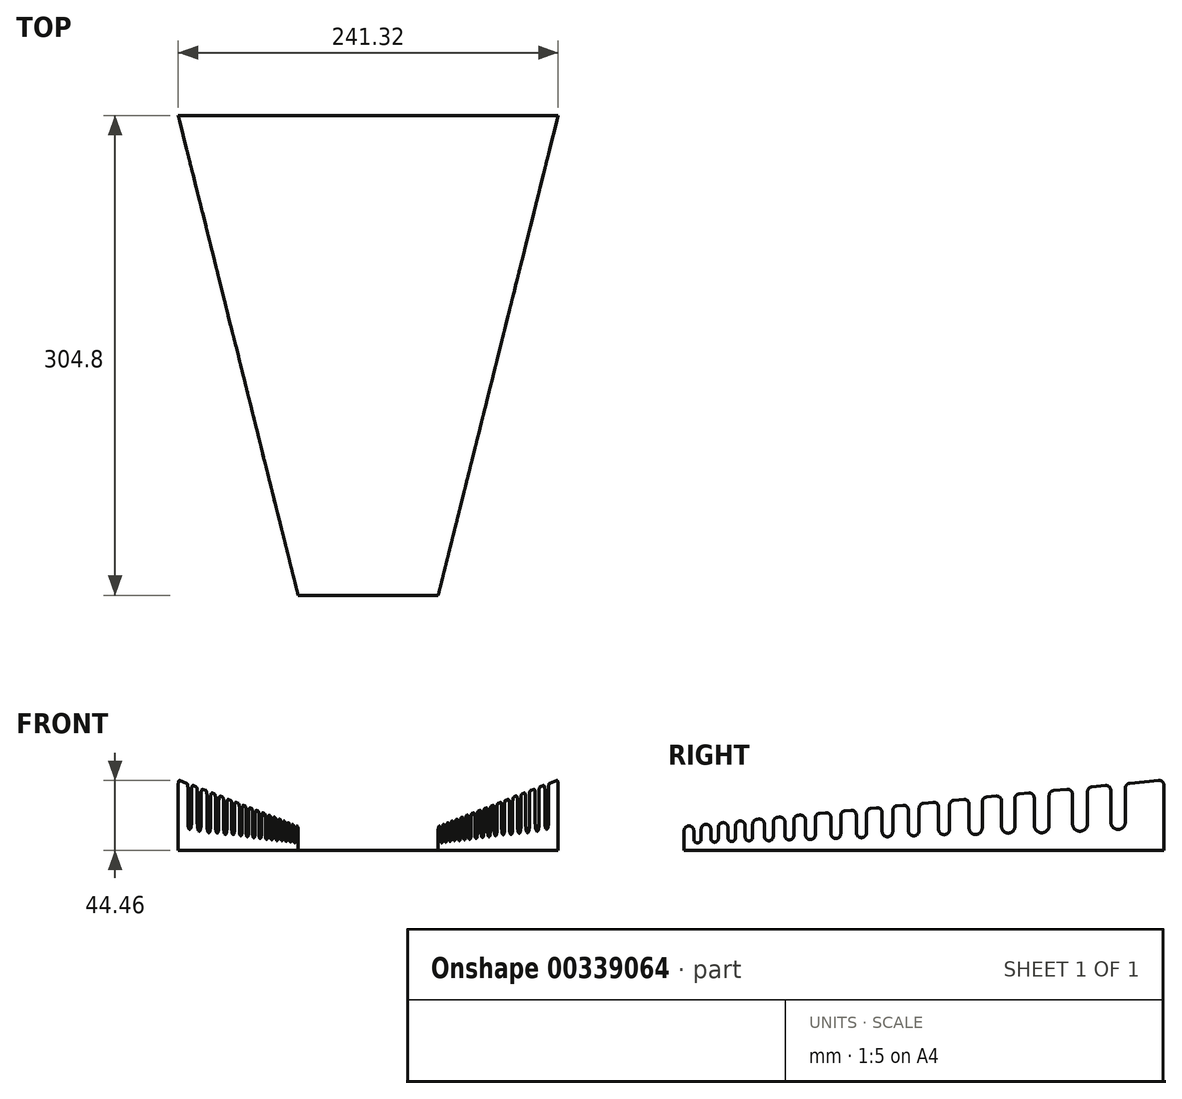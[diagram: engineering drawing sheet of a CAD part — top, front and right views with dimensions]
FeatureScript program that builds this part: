
annotation { "Feature Type Name" : "Feature", "Feature Type Description" : "" }
export const myFeature = defineFeature(function(context is Context, id is Id, definition is map)
    precondition{}
    {
        {
            var Q0;
            Q0=qCreatedBy(makeId("Top.planeOp"),FACE);
            var sketch = newSketch(context, id + "F0", { "sketchPlane" : qUnion([Q0])});
            skLineSegment(sketch, "E0", {"start": v(-44.45, 0) * mm, "end": v(44.45, 0) * mm});
            skLineSegment(sketch, "E1", {"start": v(44.45, 0) * mm, "end": v(120.65, 304.8) * mm});
            skLineSegment(sketch, "E2", {"start": v(120.65, 304.8) * mm, "end": v(-120.65, 304.8) * mm});
            skLineSegment(sketch, "E3", {"start": v(-120.65, 304.8) * mm, "end": v(-44.45, 0) * mm});
            skSolve(sketch);
        }
        {
            var Q0;
            Q0 = qSketchRegion(id + "F0", true);
            extrude(context, id + "F1", {"entities" : qUnion([Q0]), "depth" : 3 / 406.4 * mm});
        }
        {
            var Q0;
            Q0=makeQuery(id+"F1.opExtrude","SWEPT_FACE",FACE,{"disambiguationData":[OSD([sQuery(id+"F0.wireOp",EDGE,"E1")])]});
            var sketch = newSketch(context, id + "F2", { "sketchPlane" : qUnion([Q0])});
            skLineSegment(sketch, "E4", {"start": v(10.78, 0) * mm, "end": v(10.78, 12.35) * mm});
            skLineSegment(sketch, "E5", {"start": v(13.66, 15.51) * mm, "end": v(13.66, 15.51) * mm});
            skLineSegment(sketch, "E6", {"start": v(17.13, 12.35) * mm, "end": v(17.13, 7.18) * mm});
            skLineSegment(sketch, "E7", {"start": v(17.13, 7.18) * mm, "end": v(21.96, 7.37) * mm, "construction": true});
            skLineSegment(sketch, "E8", {"start": v(21.96, 7.37) * mm, "end": v(21.96, 13.4) * mm});
            skLineSegment(sketch, "E9", {"start": v(24.83, 16.56) * mm, "end": v(24.83, 16.56) * mm});
            skLineSegment(sketch, "E10", {"start": v(28.3, 13.4) * mm, "end": v(28.3, 7.62) * mm});
            skLineSegment(sketch, "E11", {"start": v(28.3, 7.62) * mm, "end": v(33.13, 7.82) * mm, "construction": true});
            skLineSegment(sketch, "E12", {"start": v(33.13, 7.82) * mm, "end": v(33.13, 14.45) * mm});
            skLineSegment(sketch, "E13", {"start": v(36.01, 17.61) * mm, "end": v(36.01, 17.61) * mm});
            skLineSegment(sketch, "E14", {"start": v(39.48, 14.45) * mm, "end": v(39.48, 8.07) * mm});
            skLineSegment(sketch, "E15", {"start": v(39.48, 8.07) * mm, "end": v(44.38, 8.27) * mm, "construction": true});
            skLineSegment(sketch, "E16", {"start": v(44.38, 8.27) * mm, "end": v(44.38, 15.5) * mm});
            skLineSegment(sketch, "E17", {"start": v(47.26, 18.67) * mm, "end": v(47.26, 18.67) * mm});
            skLineSegment(sketch, "E18", {"start": v(50.73, 15.5) * mm, "end": v(50.73, 8.52) * mm});
            skLineSegment(sketch, "E19", {"start": v(50.73, 8.52) * mm, "end": v(55.69, 8.72) * mm, "construction": true});
            skLineSegment(sketch, "E20", {"start": v(55.69, 8.72) * mm, "end": v(55.69, 16.57) * mm});
            skLineSegment(sketch, "E21", {"start": v(58.57, 19.73) * mm, "end": v(59.84, 19.85) * mm});
            skLineSegment(sketch, "E22", {"start": v(63.3, 16.7) * mm, "end": v(63.3, 9.02) * mm});
            skLineSegment(sketch, "E23", {"start": v(63.3, 9.02) * mm, "end": v(69.15, 9.26) * mm, "construction": true});
            skLineSegment(sketch, "E24", {"start": v(69.15, 9.26) * mm, "end": v(69.15, 17.84) * mm});
            skLineSegment(sketch, "E25", {"start": v(72.03, 21) * mm, "end": v(73.3, 21.12) * mm});
            skLineSegment(sketch, "E26", {"start": v(76.77, 17.96) * mm, "end": v(76.77, 9.56) * mm});
            skLineSegment(sketch, "E27", {"start": v(76.77, 9.56) * mm, "end": v(82.61, 9.8) * mm, "construction": true});
            skLineSegment(sketch, "E28", {"start": v(82.61, 9.8) * mm, "end": v(82.61, 19.1) * mm});
            skLineSegment(sketch, "E29", {"start": v(85.49, 22.26) * mm, "end": v(86.76, 22.38) * mm});
            skLineSegment(sketch, "E30", {"start": v(90.23, 19.22) * mm, "end": v(90.23, 10.1) * mm});
            skLineSegment(sketch, "E31", {"start": v(90.23, 10.1) * mm, "end": v(96.7, 10.36) * mm, "construction": true});
            skLineSegment(sketch, "E32", {"start": v(96.7, 10.36) * mm, "end": v(96.7, 20.43) * mm});
            skLineSegment(sketch, "E33", {"start": v(99.59, 23.59) * mm, "end": v(103.4, 23.95) * mm});
            skLineSegment(sketch, "E34", {"start": v(106.87, 20.79) * mm, "end": v(106.87, 10.77) * mm});
            skLineSegment(sketch, "E35", {"start": v(106.87, 10.77) * mm, "end": v(113.35, 11.02) * mm, "construction": true});
            skLineSegment(sketch, "E36", {"start": v(113.35, 11.02) * mm, "end": v(113.35, 22) * mm});
            skLineSegment(sketch, "E37", {"start": v(116.22, 25.15) * mm, "end": v(120.03, 25.51) * mm});
            skLineSegment(sketch, "E38", {"start": v(123.5, 22.35) * mm, "end": v(123.5, 11.43) * mm});
            skLineSegment(sketch, "E39", {"start": v(123.5, 11.43) * mm, "end": v(130.24, 11.7) * mm, "construction": true});
            skLineSegment(sketch, "E40", {"start": v(130.24, 11.7) * mm, "end": v(130.24, 23.58) * mm});
            skLineSegment(sketch, "E41", {"start": v(133.11, 26.74) * mm, "end": v(136.92, 27.1) * mm});
            skLineSegment(sketch, "E42", {"start": v(140.4, 23.94) * mm, "end": v(140.4, 12.1) * mm});
            skLineSegment(sketch, "E43", {"start": v(140.4, 12.1) * mm, "end": v(147.38, 12.39) * mm, "construction": true});
            skLineSegment(sketch, "E44", {"start": v(147.38, 12.39) * mm, "end": v(147.38, 25.2) * mm});
            skLineSegment(sketch, "E45", {"start": v(150.26, 28.35) * mm, "end": v(154.07, 28.71) * mm});
            skLineSegment(sketch, "E46", {"start": v(157.54, 25.55) * mm, "end": v(157.54, 12.8) * mm});
            skLineSegment(sketch, "E47", {"start": v(157.54, 12.8) * mm, "end": v(164.65, 13.08) * mm, "construction": true});
            skLineSegment(sketch, "E48", {"start": v(164.65, 13.08) * mm, "end": v(164.65, 26.82) * mm});
            skLineSegment(sketch, "E49", {"start": v(167.53, 29.98) * mm, "end": v(173.88, 30.57) * mm});
            skLineSegment(sketch, "E50", {"start": v(177.35, 27.41) * mm, "end": v(177.35, 13.59) * mm});
            skLineSegment(sketch, "E51", {"start": v(177.35, 13.59) * mm, "end": v(184.6, 13.88) * mm, "construction": true});
            skLineSegment(sketch, "E52", {"start": v(184.6, 13.88) * mm, "end": v(184.6, 28.69) * mm});
            skLineSegment(sketch, "E53", {"start": v(187.47, 31.85) * mm, "end": v(193.82, 32.45) * mm});
            skLineSegment(sketch, "E54", {"start": v(197.3, 29.29) * mm, "end": v(197.3, 14.38) * mm});
            skLineSegment(sketch, "E55", {"start": v(197.3, 14.38) * mm, "end": v(205.93, 14.73) * mm, "construction": true});
            skLineSegment(sketch, "E56", {"start": v(205.93, 14.73) * mm, "end": v(205.93, 30.7) * mm});
            skLineSegment(sketch, "E57", {"start": v(208.8, 33.86) * mm, "end": v(215.16, 34.45) * mm});
            skLineSegment(sketch, "E58", {"start": v(218.63, 31.3) * mm, "end": v(218.63, 15.24) * mm});
            skLineSegment(sketch, "E59", {"start": v(218.63, 15.24) * mm, "end": v(227.26, 15.58) * mm, "construction": true});
            skLineSegment(sketch, "E60", {"start": v(227.26, 15.58) * mm, "end": v(227.26, 32.7) * mm});
            skLineSegment(sketch, "E61", {"start": v(230.14, 35.86) * mm, "end": v(236.5, 36.46) * mm});
            skLineSegment(sketch, "E62", {"start": v(239.96, 33.3) * mm, "end": v(239.96, 16.1) * mm});
            skLineSegment(sketch, "E63", {"start": v(239.96, 16.1) * mm, "end": v(249.74, 16.48) * mm, "construction": true});
            skLineSegment(sketch, "E64", {"start": v(249.74, 16.48) * mm, "end": v(249.74, 34.81) * mm});
            skLineSegment(sketch, "E65", {"start": v(252.62, 37.98) * mm, "end": v(261.51, 38.81) * mm});
            skLineSegment(sketch, "E66", {"start": v(264.98, 35.65) * mm, "end": v(264.98, 17.1) * mm});
            skLineSegment(sketch, "E67", {"start": v(264.98, 17.1) * mm, "end": v(274.89, 17.49) * mm, "construction": true});
            skLineSegment(sketch, "E68", {"start": v(274.89, 17.49) * mm, "end": v(274.89, 37.18) * mm});
            skLineSegment(sketch, "E69", {"start": v(277.77, 40.34) * mm, "end": v(286.66, 41.18) * mm});
            skLineSegment(sketch, "E70", {"start": v(290.13, 38.01) * mm, "end": v(290.13, 18.1) * mm});
            skLineSegment(sketch, "E71", {"start": v(290.13, 18.1) * mm, "end": v(299.65, 18.48) * mm, "construction": true});
            skLineSegment(sketch, "E72", {"start": v(299.65, 18.48) * mm, "end": v(299.65, 39.5) * mm});
            skLineSegment(sketch, "E73", {"start": v(265.9, 39.22) * mm, "end": v(265.9, 39.22) * mm});
            skLineSegment(sketch, "E74", {"start": v(324.96, 41.29) * mm, "end": v(324.96, 0) * mm});
            skArc(sketch, "E75", {"start": v(17.13, 7.18) * mm, "mid": v(19.64, 4.76) * mm, "end": v(21.96, 7.37) * mm});
            skArc(sketch, "E76", {"start": v(28.3, 7.62) * mm, "mid": v(30.82, 5.2) * mm, "end": v(33.13, 7.82) * mm});
            skArc(sketch, "E77", {"start": v(39.48, 8.07) * mm, "mid": v(42.04, 5.62) * mm, "end": v(44.38, 8.27) * mm});
            skArc(sketch, "E78", {"start": v(50.73, 8.52) * mm, "mid": v(53.31, 6.04) * mm, "end": v(55.69, 8.72) * mm});
            skArc(sketch, "E79", {"start": v(63.3, 9.02) * mm, "mid": v(66.35, 6.1) * mm, "end": v(69.15, 9.26) * mm});
            skArc(sketch, "E80", {"start": v(76.77, 9.56) * mm, "mid": v(79.81, 6.64) * mm, "end": v(82.61, 9.8) * mm});
            skArc(sketch, "E81", {"start": v(90.23, 10.1) * mm, "mid": v(93.6, 6.86) * mm, "end": v(96.7, 10.36) * mm});
            skArc(sketch, "E82", {"start": v(106.87, 10.77) * mm, "mid": v(110.24, 7.52) * mm, "end": v(113.35, 11.02) * mm});
            skArc(sketch, "E83", {"start": v(123.5, 11.43) * mm, "mid": v(127.01, 8.06) * mm, "end": v(130.24, 11.7) * mm});
            skArc(sketch, "E84", {"start": v(140.4, 12.1) * mm, "mid": v(144.03, 8.61) * mm, "end": v(147.38, 12.39) * mm});
            skArc(sketch, "E85", {"start": v(157.54, 12.8) * mm, "mid": v(161.25, 9.23) * mm, "end": v(164.65, 13.08) * mm});
            skArc(sketch, "E86", {"start": v(177.35, 13.59) * mm, "mid": v(181.12, 9.96) * mm, "end": v(184.6, 13.88) * mm});
            skArc(sketch, "E87", {"start": v(197.3, 14.38) * mm, "mid": v(201.8, 10.06) * mm, "end": v(205.93, 14.73) * mm});
            skArc(sketch, "E88", {"start": v(218.63, 15.24) * mm, "mid": v(223.13, 10.92) * mm, "end": v(227.26, 15.58) * mm});
            skArc(sketch, "E89", {"start": v(239.96, 16.1) * mm, "mid": v(245.06, 11.2) * mm, "end": v(249.74, 16.48) * mm});
            skArc(sketch, "E90", {"start": v(264.98, 17.1) * mm, "mid": v(270.14, 12.13) * mm, "end": v(274.89, 17.49) * mm});
            skArc(sketch, "E91", {"start": v(290.13, 18.1) * mm, "mid": v(295.1, 13.33) * mm, "end": v(299.65, 18.48) * mm});
            skArc(sketch, "E92.filletArc", {"start": v(324.96, 41.29) * mm, "mid": v(323.92, 43.64) * mm, "end": v(321.49, 44.45) * mm});
            skArc(sketch, "E93.filletArc", {"start": v(302.53, 42.67) * mm, "mid": v(300.48, 41.64) * mm, "end": v(299.65, 39.5) * mm});
            skPoint(sketch, "E94.visualSharp", {"position": v(290.13, 41.5) * mm});
            skArc(sketch, "E94.filletArc", {"start": v(290.13, 38.01) * mm, "mid": v(289.1, 40.36) * mm, "end": v(286.66, 41.18) * mm});
            skPoint(sketch, "E95.visualSharp", {"position": v(274.89, 40.07) * mm});
            skArc(sketch, "E95.filletArc", {"start": v(277.77, 40.34) * mm, "mid": v(275.72, 39.32) * mm, "end": v(274.89, 37.18) * mm});
            skPoint(sketch, "E96.visualSharp", {"position": v(264.98, 39.14) * mm});
            skArc(sketch, "E96.filletArc", {"start": v(264.98, 35.65) * mm, "mid": v(263.95, 38) * mm, "end": v(261.51, 38.81) * mm});
            skPoint(sketch, "E97.visualSharp", {"position": v(249.74, 37.7) * mm});
            skArc(sketch, "E97.filletArc", {"start": v(252.62, 37.98) * mm, "mid": v(250.57, 36.95) * mm, "end": v(249.74, 34.81) * mm});
            skPoint(sketch, "E98.visualSharp", {"position": v(239.96, 36.79) * mm});
            skArc(sketch, "E98.filletArc", {"start": v(239.96, 33.3) * mm, "mid": v(238.93, 35.65) * mm, "end": v(236.5, 36.46) * mm});
            skPoint(sketch, "E99.visualSharp", {"position": v(227.26, 35.6) * mm});
            skArc(sketch, "E99.filletArc", {"start": v(230.14, 35.86) * mm, "mid": v(228.1, 34.84) * mm, "end": v(227.26, 32.7) * mm});
            skPoint(sketch, "E100.visualSharp", {"position": v(218.63, 34.78) * mm});
            skArc(sketch, "E100.filletArc", {"start": v(218.63, 31.3) * mm, "mid": v(217.6, 33.64) * mm, "end": v(215.16, 34.45) * mm});
            skPoint(sketch, "E101.visualSharp", {"position": v(205.93, 33.59) * mm});
            skArc(sketch, "E101.filletArc", {"start": v(208.8, 33.86) * mm, "mid": v(206.76, 32.83) * mm, "end": v(205.93, 30.7) * mm});
            skPoint(sketch, "E102.visualSharp", {"position": v(197.3, 32.77) * mm});
            skArc(sketch, "E102.filletArc", {"start": v(197.3, 29.29) * mm, "mid": v(196.26, 31.63) * mm, "end": v(193.82, 32.45) * mm});
            skPoint(sketch, "E103.visualSharp", {"position": v(184.6, 31.58) * mm});
            skArc(sketch, "E103.filletArc", {"start": v(187.47, 31.85) * mm, "mid": v(185.42, 30.83) * mm, "end": v(184.6, 28.69) * mm});
            skPoint(sketch, "E104.visualSharp", {"position": v(177.35, 30.9) * mm});
            skArc(sketch, "E104.filletArc", {"start": v(177.35, 27.41) * mm, "mid": v(176.32, 29.76) * mm, "end": v(173.88, 30.57) * mm});
            skPoint(sketch, "E105.visualSharp", {"position": v(164.65, 29.7) * mm});
            skArc(sketch, "E105.filletArc", {"start": v(167.53, 29.98) * mm, "mid": v(165.48, 28.95) * mm, "end": v(164.65, 26.82) * mm});
            skPoint(sketch, "E106.visualSharp", {"position": v(157.54, 29.04) * mm});
            skArc(sketch, "E106.filletArc", {"start": v(157.54, 25.55) * mm, "mid": v(156.5, 27.9) * mm, "end": v(154.07, 28.71) * mm});
            skPoint(sketch, "E107.visualSharp", {"position": v(147.38, 28.08) * mm});
            skArc(sketch, "E107.filletArc", {"start": v(150.26, 28.35) * mm, "mid": v(148.2, 27.33) * mm, "end": v(147.38, 25.2) * mm});
            skPoint(sketch, "E108.visualSharp", {"position": v(140.4, 27.43) * mm});
            skArc(sketch, "E108.filletArc", {"start": v(140.4, 23.94) * mm, "mid": v(139.36, 26.29) * mm, "end": v(136.92, 27.1) * mm});
            skPoint(sketch, "E109.visualSharp", {"position": v(130.24, 26.47) * mm});
            skArc(sketch, "E109.filletArc", {"start": v(133.11, 26.74) * mm, "mid": v(131.06, 25.72) * mm, "end": v(130.24, 23.58) * mm});
            skPoint(sketch, "E110.visualSharp", {"position": v(123.5, 25.84) * mm});
            skArc(sketch, "E110.filletArc", {"start": v(123.5, 22.35) * mm, "mid": v(122.47, 24.7) * mm, "end": v(120.03, 25.51) * mm});
            skPoint(sketch, "E111.visualSharp", {"position": v(113.35, 24.88) * mm});
            skArc(sketch, "E111.filletArc", {"start": v(116.22, 25.15) * mm, "mid": v(114.17, 24.13) * mm, "end": v(113.35, 22) * mm});
            skPoint(sketch, "E112.visualSharp", {"position": v(106.87, 24.27) * mm});
            skArc(sketch, "E112.filletArc", {"start": v(106.87, 20.79) * mm, "mid": v(105.83, 23.13) * mm, "end": v(103.4, 23.95) * mm});
            skPoint(sketch, "E113.visualSharp", {"position": v(96.7, 23.32) * mm});
            skArc(sketch, "E113.filletArc", {"start": v(99.59, 23.59) * mm, "mid": v(97.54, 22.57) * mm, "end": v(96.7, 20.43) * mm});
            skPoint(sketch, "E114.visualSharp", {"position": v(90.23, 22.7) * mm});
            skArc(sketch, "E114.filletArc", {"start": v(90.23, 19.22) * mm, "mid": v(89.2, 21.57) * mm, "end": v(86.76, 22.38) * mm});
            skPoint(sketch, "E115.visualSharp", {"position": v(82.61, 22) * mm});
            skArc(sketch, "E115.filletArc", {"start": v(85.49, 22.26) * mm, "mid": v(83.44, 21.24) * mm, "end": v(82.61, 19.1) * mm});
            skPoint(sketch, "E116.visualSharp", {"position": v(76.77, 21.44) * mm});
            skArc(sketch, "E116.filletArc", {"start": v(76.77, 17.96) * mm, "mid": v(75.73, 20.3) * mm, "end": v(73.3, 21.12) * mm});
            skPoint(sketch, "E117.visualSharp", {"position": v(69.15, 20.73) * mm});
            skArc(sketch, "E117.filletArc", {"start": v(72.03, 21) * mm, "mid": v(69.98, 19.97) * mm, "end": v(69.15, 17.84) * mm});
            skPoint(sketch, "E118.visualSharp", {"position": v(63.3, 20.18) * mm});
            skArc(sketch, "E118.filletArc", {"start": v(63.3, 16.7) * mm, "mid": v(62.27, 19.04) * mm, "end": v(59.84, 19.85) * mm});
            skPoint(sketch, "E119.visualSharp", {"position": v(55.69, 19.46) * mm});
            skArc(sketch, "E119.filletArc", {"start": v(58.57, 19.73) * mm, "mid": v(56.52, 18.7) * mm, "end": v(55.69, 16.57) * mm});
            skPoint(sketch, "E120.visualSharp", {"position": v(50.73, 19) * mm});
            skArc(sketch, "E120.filletArc", {"start": v(50.73, 15.5) * mm, "mid": v(49.7, 17.86) * mm, "end": v(47.26, 18.67) * mm});
            skPoint(sketch, "E121.visualSharp", {"position": v(44.38, 18.4) * mm});
            skArc(sketch, "E121.filletArc", {"start": v(47.26, 18.67) * mm, "mid": v(45.21, 17.65) * mm, "end": v(44.38, 15.5) * mm});
            skPoint(sketch, "E122.visualSharp", {"position": v(39.48, 17.94) * mm});
            skArc(sketch, "E122.filletArc", {"start": v(39.48, 14.45) * mm, "mid": v(38.45, 16.8) * mm, "end": v(36.01, 17.61) * mm});
            skPoint(sketch, "E123.visualSharp", {"position": v(33.13, 17.34) * mm});
            skArc(sketch, "E123.filletArc", {"start": v(36.01, 17.61) * mm, "mid": v(33.96, 16.59) * mm, "end": v(33.13, 14.45) * mm});
            skPoint(sketch, "E124.visualSharp", {"position": v(28.3, 16.89) * mm});
            skArc(sketch, "E124.filletArc", {"start": v(28.3, 13.4) * mm, "mid": v(27.27, 15.75) * mm, "end": v(24.83, 16.56) * mm});
            skPoint(sketch, "E125.visualSharp", {"position": v(21.96, 16.3) * mm});
            skArc(sketch, "E125.filletArc", {"start": v(24.83, 16.56) * mm, "mid": v(22.78, 15.54) * mm, "end": v(21.96, 13.4) * mm});
            skPoint(sketch, "E126.visualSharp", {"position": v(17.13, 15.84) * mm});
            skArc(sketch, "E126.filletArc", {"start": v(17.13, 12.35) * mm, "mid": v(16.1, 14.7) * mm, "end": v(13.66, 15.51) * mm});
            skPoint(sketch, "E127.visualSharp", {"position": v(10.78, 15.24) * mm});
            skArc(sketch, "E127.filletArc", {"start": v(13.66, 15.51) * mm, "mid": v(11.6, 14.49) * mm, "end": v(10.78, 12.35) * mm});
            skLineSegment(sketch, "E128", {"start": v(10.78, 0) * mm, "end": v(324.96, 0) * mm});
            skLineSegment(sketch, "E129", {"start": v(321.49, 44.45) * mm, "end": v(302.53, 42.67) * mm});
            skSolve(sketch);
        }
        {
            var Q0;
            Q0 = qSketchRegion(id + "F2", true);
            extrude(context, id + "F3", {"entities" : qUnion([Q0]), "depth" : 3 / 406.4 * mm});
        }
        {
            var Q0;
            Q0=makeQuery(id+"F3.opExtrude","SWEPT_BODY",BODY,{"disambiguationData":[OSD([sQuery(id+"F2.wireOp",EDGE,"E4"),sQuery(id+"F2.wireOp",EDGE,"E5"),sQuery(id+"F2.wireOp",EDGE,"E6"),sQuery(id+"F2.wireOp",EDGE,"E8"),sQuery(id+"F2.wireOp",EDGE,"E9"),sQuery(id+"F2.wireOp",EDGE,"E10"),sQuery(id+"F2.wireOp",EDGE,"E12"),sQuery(id+"F2.wireOp",EDGE,"E13"),sQuery(id+"F2.wireOp",EDGE,"E14"),sQuery(id+"F2.wireOp",EDGE,"E16"),sQuery(id+"F2.wireOp",EDGE,"E17"),sQuery(id+"F2.wireOp",EDGE,"E18"),sQuery(id+"F2.wireOp",EDGE,"E20"),sQuery(id+"F2.wireOp",EDGE,"E21"),sQuery(id+"F2.wireOp",EDGE,"E22"),sQuery(id+"F2.wireOp",EDGE,"E24"),sQuery(id+"F2.wireOp",EDGE,"E25"),sQuery(id+"F2.wireOp",EDGE,"E26"),sQuery(id+"F2.wireOp",EDGE,"E28"),sQuery(id+"F2.wireOp",EDGE,"E29"),sQuery(id+"F2.wireOp",EDGE,"E30"),sQuery(id+"F2.wireOp",EDGE,"E32"),sQuery(id+"F2.wireOp",EDGE,"E33"),sQuery(id+"F2.wireOp",EDGE,"E34"),sQuery(id+"F2.wireOp",EDGE,"E36"),sQuery(id+"F2.wireOp",EDGE,"E37"),sQuery(id+"F2.wireOp",EDGE,"E38"),sQuery(id+"F2.wireOp",EDGE,"E40"),sQuery(id+"F2.wireOp",EDGE,"E41"),sQuery(id+"F2.wireOp",EDGE,"E42"),sQuery(id+"F2.wireOp",EDGE,"E44"),sQuery(id+"F2.wireOp",EDGE,"E45"),sQuery(id+"F2.wireOp",EDGE,"E46"),sQuery(id+"F2.wireOp",EDGE,"E48"),sQuery(id+"F2.wireOp",EDGE,"E49"),sQuery(id+"F2.wireOp",EDGE,"E50"),sQuery(id+"F2.wireOp",EDGE,"E52"),sQuery(id+"F2.wireOp",EDGE,"E53"),sQuery(id+"F2.wireOp",EDGE,"E54"),sQuery(id+"F2.wireOp",EDGE,"E56"),sQuery(id+"F2.wireOp",EDGE,"E57"),sQuery(id+"F2.wireOp",EDGE,"E58"),sQuery(id+"F2.wireOp",EDGE,"E60"),sQuery(id+"F2.wireOp",EDGE,"E61"),sQuery(id+"F2.wireOp",EDGE,"E62"),sQuery(id+"F2.wireOp",EDGE,"E64"),sQuery(id+"F2.wireOp",EDGE,"E65"),sQuery(id+"F2.wireOp",EDGE,"E66"),sQuery(id+"F2.wireOp",EDGE,"E68"),sQuery(id+"F2.wireOp",EDGE,"E70"),sQuery(id+"F2.wireOp",EDGE,"E72"),sQuery(id+"F2.wireOp",EDGE,"9ihwAVwL-yMMt-xmYE-Td51-ayaX15x94NwS"),sQuery(id+"F2.wireOp",EDGE,"6Wx5teZL-wODt-y5db-ANnT-UPmmfWM3Ukpe"),sQuery(id+"F2.wireOp",EDGE,"E85TSMDE-1efA-kweR-pmmq-KC4Xdjg828U5"),sQuery(id+"F2.wireOp",EDGE,"NmcfjtNE-oIZ5-0b0F-BYqz-Lg2e0aJrtCXq"),sQuery(id+"F2.wireOp",EDGE,"dxBorZXQ-VSEu-lgl5-VqOv-JdW7uacsbKmT"),sQuery(id+"F2.wireOp",EDGE,"7qnZEuvj-AQxg-qu0J-dGde-6bTH4GPdGrSV"),sQuery(id+"F2.wireOp",EDGE,"yVdPXEXH-w7M2-4kCM-5lBI-aBlkXL1ZHiPJ"),sQuery(id+"F2.wireOp",EDGE,"aQqWlaiA-IXy9-PBNe-gHCr-Hn8R57gy5fic"),sQuery(id+"F2.wireOp",EDGE,"6GCAIcDh-OiFF-jA3G-d8kp-Ck2v8U8bEO0u"),sQuery(id+"F2.wireOp",EDGE,"Da3AZwT8-KkLN-pfs7-XyQb-8dlWgiG0dyCa"),sQuery(id+"F2.wireOp",EDGE,"kZRNVZUt-hahL-Bpj9-GCHh-G2hXmQbwK9aH"),sQuery(id+"F2.wireOp",EDGE,"LzEq5xnF-NvSS-PmON-YUBG-ChX3msSRTm2m"),sQuery(id+"F2.wireOp",EDGE,"wfnGJh9B-PpQ6-th6Y-06zF-Opqufyt59sBU"),sQuery(id+"F2.wireOp",EDGE,"fs9keDXd-eg4m-qbRe-etzE-jeHQbsrzH9p6"),sQuery(id+"F2.wireOp",EDGE,"E74"),sQuery(id+"F2.wireOp",EDGE,"E75"),sQuery(id+"F2.wireOp",EDGE,"E76"),sQuery(id+"F2.wireOp",EDGE,"E77"),sQuery(id+"F2.wireOp",EDGE,"E78"),sQuery(id+"F2.wireOp",EDGE,"E79"),sQuery(id+"F2.wireOp",EDGE,"E80"),sQuery(id+"F2.wireOp",EDGE,"E81"),sQuery(id+"F2.wireOp",EDGE,"E82"),sQuery(id+"F2.wireOp",EDGE,"E83"),sQuery(id+"F2.wireOp",EDGE,"E84"),sQuery(id+"F2.wireOp",EDGE,"E85"),sQuery(id+"F2.wireOp",EDGE,"E86"),sQuery(id+"F2.wireOp",EDGE,"E87"),sQuery(id+"F2.wireOp",EDGE,"E88"),sQuery(id+"F2.wireOp",EDGE,"E89"),sQuery(id+"F2.wireOp",EDGE,"E90"),sQuery(id+"F2.wireOp",EDGE,"E91"),sQuery(id+"F2.wireOp",EDGE,"51521edc-c36c-4741-a2c8-e6c89847c520"),sQuery(id+"F2.wireOp",EDGE,"c2937420-2c0e-48e4-a297-3b46329f77ed"),sQuery(id+"F2.wireOp",EDGE,"e09dc18e-cf75-4063-a493-89d788ca84c7"),sQuery(id+"F2.wireOp",EDGE,"7a65d38f-d6da-4d3c-822c-5ff490d6cca7"),sQuery(id+"F2.wireOp",EDGE,"786f9d07-c6b8-49c3-99dd-2390568de801"),sQuery(id+"F2.wireOp",EDGE,"E92.filletArc"),sQuery(id+"F2.wireOp",EDGE,"5ea56c1c-ad5f-49d5-96a2-adc58262b3a1.filletArc"),sQuery(id+"F2.wireOp",EDGE,"0aeb03af-12b2-408e-9093-31f995c1a81d.filletArc"),sQuery(id+"F2.wireOp",EDGE,"8812127d-24f4-4bd0-9dec-8077494d4ccb.filletArc"),sQuery(id+"F2.wireOp",EDGE,"cbbaf091-34e9-40b3-b33f-ebed252aad49.filletArc"),sQuery(id+"F2.wireOp",EDGE,"6c4703d3-6c70-417a-8b8e-03f95a004045.filletArc"),sQuery(id+"F2.wireOp",EDGE,"8acad820-d952-4f21-b7f7-e183264cdb16.filletArc"),sQuery(id+"F2.wireOp",EDGE,"bafa3667-eccb-4ae8-90a9-cd3a36b324d0.filletArc"),sQuery(id+"F2.wireOp",EDGE,"a5abbfff-01b3-455a-8b0d-a460608581f8.filletArc"),sQuery(id+"F2.wireOp",EDGE,"af9c7569-dde1-4ec6-9877-167f455a3e9a.filletArc"),sQuery(id+"F2.wireOp",EDGE,"d1f913c9-b633-4928-9db4-b2b14fc9df0b.filletArc"),sQuery(id+"F2.wireOp",EDGE,"E93.filletArc"),sQuery(id+"F2.wireOp",EDGE,"E94.filletArc"),sQuery(id+"F2.wireOp",EDGE,"E95.filletArc"),sQuery(id+"F2.wireOp",EDGE,"E96.filletArc"),sQuery(id+"F2.wireOp",EDGE,"E97.filletArc"),sQuery(id+"F2.wireOp",EDGE,"E98.filletArc"),sQuery(id+"F2.wireOp",EDGE,"E99.filletArc"),sQuery(id+"F2.wireOp",EDGE,"E100.filletArc"),sQuery(id+"F2.wireOp",EDGE,"E101.filletArc"),sQuery(id+"F2.wireOp",EDGE,"E102.filletArc"),sQuery(id+"F2.wireOp",EDGE,"E103.filletArc"),sQuery(id+"F2.wireOp",EDGE,"E104.filletArc"),sQuery(id+"F2.wireOp",EDGE,"E105.filletArc"),sQuery(id+"F2.wireOp",EDGE,"E106.filletArc"),sQuery(id+"F2.wireOp",EDGE,"E107.filletArc"),sQuery(id+"F2.wireOp",EDGE,"E108.filletArc"),sQuery(id+"F2.wireOp",EDGE,"E109.filletArc"),sQuery(id+"F2.wireOp",EDGE,"E110.filletArc"),sQuery(id+"F2.wireOp",EDGE,"E111.filletArc"),sQuery(id+"F2.wireOp",EDGE,"E112.filletArc"),sQuery(id+"F2.wireOp",EDGE,"E113.filletArc"),sQuery(id+"F2.wireOp",EDGE,"E114.filletArc"),sQuery(id+"F2.wireOp",EDGE,"E115.filletArc"),sQuery(id+"F2.wireOp",EDGE,"E116.filletArc"),sQuery(id+"F2.wireOp",EDGE,"E117.filletArc"),sQuery(id+"F2.wireOp",EDGE,"E118.filletArc"),sQuery(id+"F2.wireOp",EDGE,"E119.filletArc"),sQuery(id+"F2.wireOp",EDGE,"E120.filletArc"),sQuery(id+"F2.wireOp",EDGE,"E121.filletArc"),sQuery(id+"F2.wireOp",EDGE,"E122.filletArc"),sQuery(id+"F2.wireOp",EDGE,"E123.filletArc"),sQuery(id+"F2.wireOp",EDGE,"E124.filletArc"),sQuery(id+"F2.wireOp",EDGE,"E125.filletArc"),sQuery(id+"F2.wireOp",EDGE,"E126.filletArc"),sQuery(id+"F2.wireOp",EDGE,"E127.filletArc"),sQuery(id+"F2.wireOp",EDGE,"E128")])]});
            var Q1;
            Q1=qCreatedBy(makeId("Right.planeOp"),FACE);
            mirror(context, id + "F4", {"operationType" : NewBodyOperationType.ADD, "entities" : qUnion([Q0]), "mirrorPlane" : qUnion([Q1])});
        }
    });
